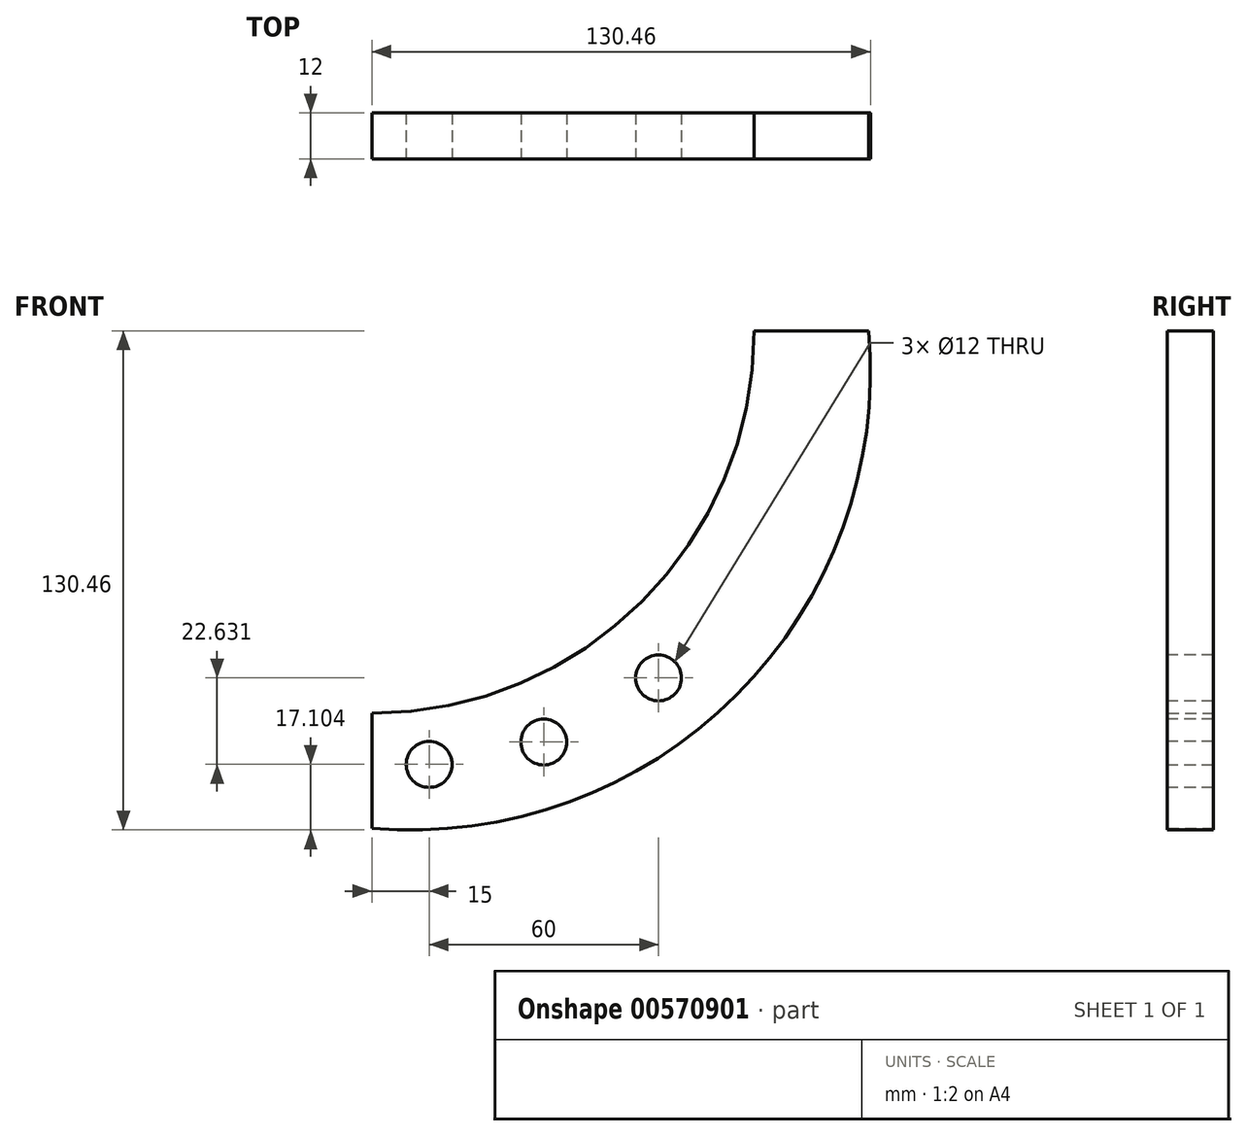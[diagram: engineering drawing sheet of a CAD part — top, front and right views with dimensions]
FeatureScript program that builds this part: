
annotation { "Feature Type Name" : "Feature", "Feature Type Description" : "" }
export const myFeature = defineFeature(function(context is Context, id is Id, definition is map)
    precondition{}
    {
        {
            var Q0;
            Q0=qCreatedBy(makeId("Front.planeOp"),FACE);
            var sketch = newSketch(context, id + "F0", { "sketchPlane" : qUnion([Q0])});
            skArc(sketch, "E0", {"start": v(0, -130) * mm, "mid": v(95.3, -95.3) * mm, "end": v(130, 0) * mm});
            skLineSegment(sketch, "E1", {"start": v(130, 0) * mm, "end": v(100, 0) * mm});
            skLineSegment(sketch, "E2", {"start": v(0, -130) * mm, "end": v(0, -100) * mm});
            skArc(sketch, "E3", {"start": v(0, -100) * mm, "mid": v(70.71, -70.71) * mm, "end": v(100, 0) * mm});
            skSolve(sketch);
        }
        {
            var Q0;
            Q0 = qSketchRegion(id + "F0", true);
            extrude(context, id + "F1", {"entities" : qUnion([Q0]), "depth" : 12 * mm, "offsetDistance" : 25 * mm});
        }
        {
            var Q0;
            Q0=makeQuery(id+"F1.opExtrude","CAP_FACE",FACE,{"disambiguationData":[OSD([sQuery(id+"F0.wireOp",EDGE,"E0"),sQuery(id+"F0.wireOp",EDGE,"E1"),sQuery(id+"F0.wireOp",EDGE,"E2"),sQuery(id+"F0.wireOp",EDGE,"E3")])],"isStart":false});
            var sketch = newSketch(context, id + "F2", { "sketchPlane" : qUnion([Q0])});
            skCircle(sketch, "E4", {"center": v(15, -113.36) * mm, "radius": 6 * mm});
            skCircle(sketch, "E5", {"center": v(45, -107.5) * mm, "radius": 6 * mm});
            skCircle(sketch, "E6", {"center": v(75, -90.73) * mm, "radius": 6 * mm});
            skSolve(sketch);
        }
        {
            var Q0;
            Q0 = qSketchRegion(id + "F2", true);
            extrude(context, id + "F3", {"entities" : qUnion([Q0]), "operationType" : NewBodyOperationType.REMOVE, "oppositeDirection" : true, "depth" : 25 * mm, "offsetDistance" : 25 * mm});
        }
    });
